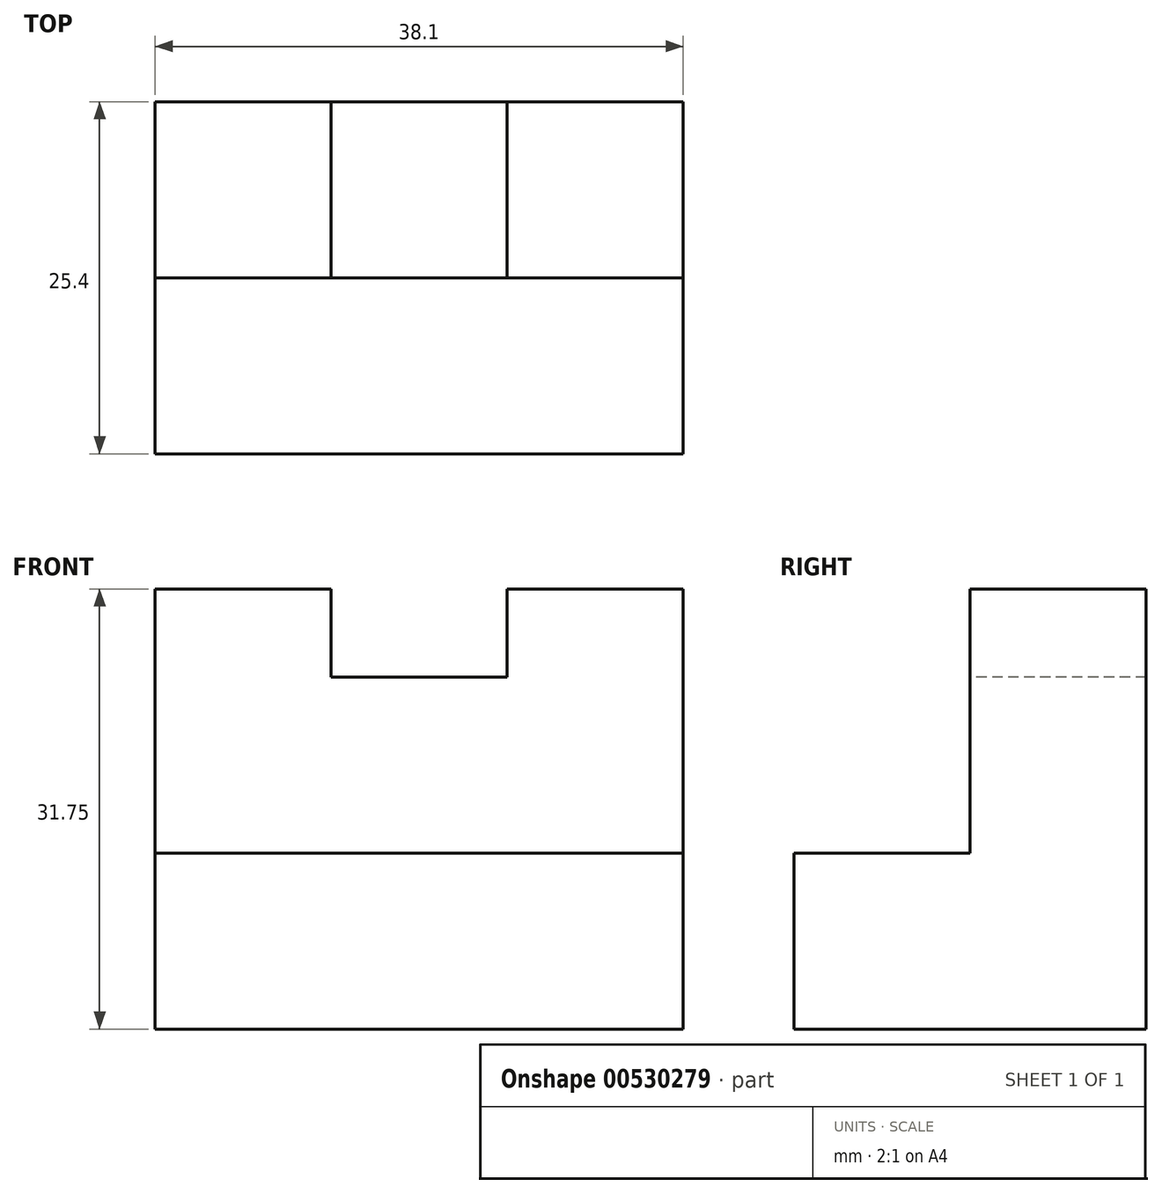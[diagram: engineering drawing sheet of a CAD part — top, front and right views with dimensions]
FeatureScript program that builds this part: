
annotation { "Feature Type Name" : "Feature", "Feature Type Description" : "" }
export const myFeature = defineFeature(function(context is Context, id is Id, definition is map)
    precondition{}
    {
        {
            var Q0;
            Q0=qCreatedBy(makeId("Front.planeOp"),FACE);
            var sketch = newSketch(context, id + "F0", { "sketchPlane" : qUnion([Q0])});
            skLineSegment(sketch, "E0", {"start": v(-46.48, 31.75) * mm, "end": v(-46.48, 0) * mm});
            skLineSegment(sketch, "E1", {"start": v(-46.48, 0) * mm, "end": v(-8.38, 0) * mm});
            skLineSegment(sketch, "E2", {"start": v(-8.38, 0) * mm, "end": v(-8.38, 31.75) * mm});
            skLineSegment(sketch, "E3", {"start": v(-8.38, 31.75) * mm, "end": v(-46.48, 31.75) * mm});
            skSolve(sketch);
        }
        {
            var Q0;
            Q0=makeQuery(id+"F0.imprint","IMPRINT",FACE,{"disambiguationData":[TD([[makeQuery(id+"F0.imprint","IMPRINT",EDGE,{"derivedFrom":sQuery(id+"F0.wireOp",EDGE,"E0")}),1.0]])]});
            extrude(context, id + "F1", {"entities" : qUnion([Q0]), "depth" : 25.4 * mm, "offsetDistance" : 25.4 * mm});
        }
        {
            var Q0;
            Q0=makeQuery(id+"F1.opExtrude","CAP_FACE",FACE,{"disambiguationData":[OSD([sQuery(id+"F0.wireOp",EDGE,"E0"),sQuery(id+"F0.wireOp",EDGE,"E1"),sQuery(id+"F0.wireOp",EDGE,"E2"),sQuery(id+"F0.wireOp",EDGE,"E3")])],"isStart":false});
            var sketch = newSketch(context, id + "F2", { "sketchPlane" : qUnion([Q0])});
            skLineSegment(sketch, "E4", {"start": v(-46.48, 12.7) * mm, "end": v(-8.38, 12.7) * mm});
            skSolve(sketch);
        }
        {
            var Q0;
            {var subQ0=sQuery(id+"F2.wireOp",EDGE,"E4");Q0=makeQuery(id+"F2.imprint","IMPRINT",FACE,{"disambiguationData":[TD([[makeQuery(id+"F2.imprint","IMPRINT",EDGE,{"derivedFrom":subQ0}),1.0]])]});}
            extrude(context, id + "F3", {"entities" : qUnion([Q0]), "operationType" : NewBodyOperationType.REMOVE, "oppositeDirection" : true, "depth" : 12.7 * mm, "offsetDistance" : 25.4 * mm});
        }
        {
            var Q0;
            Q0=makeQuery(id+"F3.boolean.opBoolean","COPY",FACE,{"derivedFrom":makeQuery(id+"F3.opExtrude","CAP_FACE",FACE,{"disambiguationData":[OSD([sQuery(id+"F0.wireOp",EDGE,"E0"),sQuery(id+"F0.wireOp",EDGE,"E2"),sQuery(id+"F0.wireOp",EDGE,"E3"),sQuery(id+"F2.wireOp",EDGE,"E4")])],"isStart":false})});
            var sketch = newSketch(context, id + "F4", { "sketchPlane" : qUnion([Q0])});
            skLineSegment(sketch, "E5", {"start": v(-33.78, 31.75) * mm, "end": v(-33.78, 25.4) * mm});
            skLineSegment(sketch, "E6", {"start": v(-21.08, 31.75) * mm, "end": v(-21.08, 25.4) * mm});
            skLineSegment(sketch, "E7", {"start": v(-33.78, 25.4) * mm, "end": v(-21.08, 25.4) * mm});
            skSolve(sketch);
        }
        {
            var Q0;
            {var subQ0=sQuery(id+"F4.wireOp",EDGE,"E5");Q0=makeQuery(id+"F4.imprint","IMPRINT",FACE,{"disambiguationData":[TD([[makeQuery(id+"F4.imprint","IMPRINT",EDGE,{"derivedFrom":subQ0}),1.0]])]});}
            extrude(context, id + "F5", {"entities" : qUnion([Q0]), "operationType" : NewBodyOperationType.REMOVE, "oppositeDirection" : true, "depth" : 25.4 * mm, "offsetDistance" : 25.4 * mm});
        }
    });
